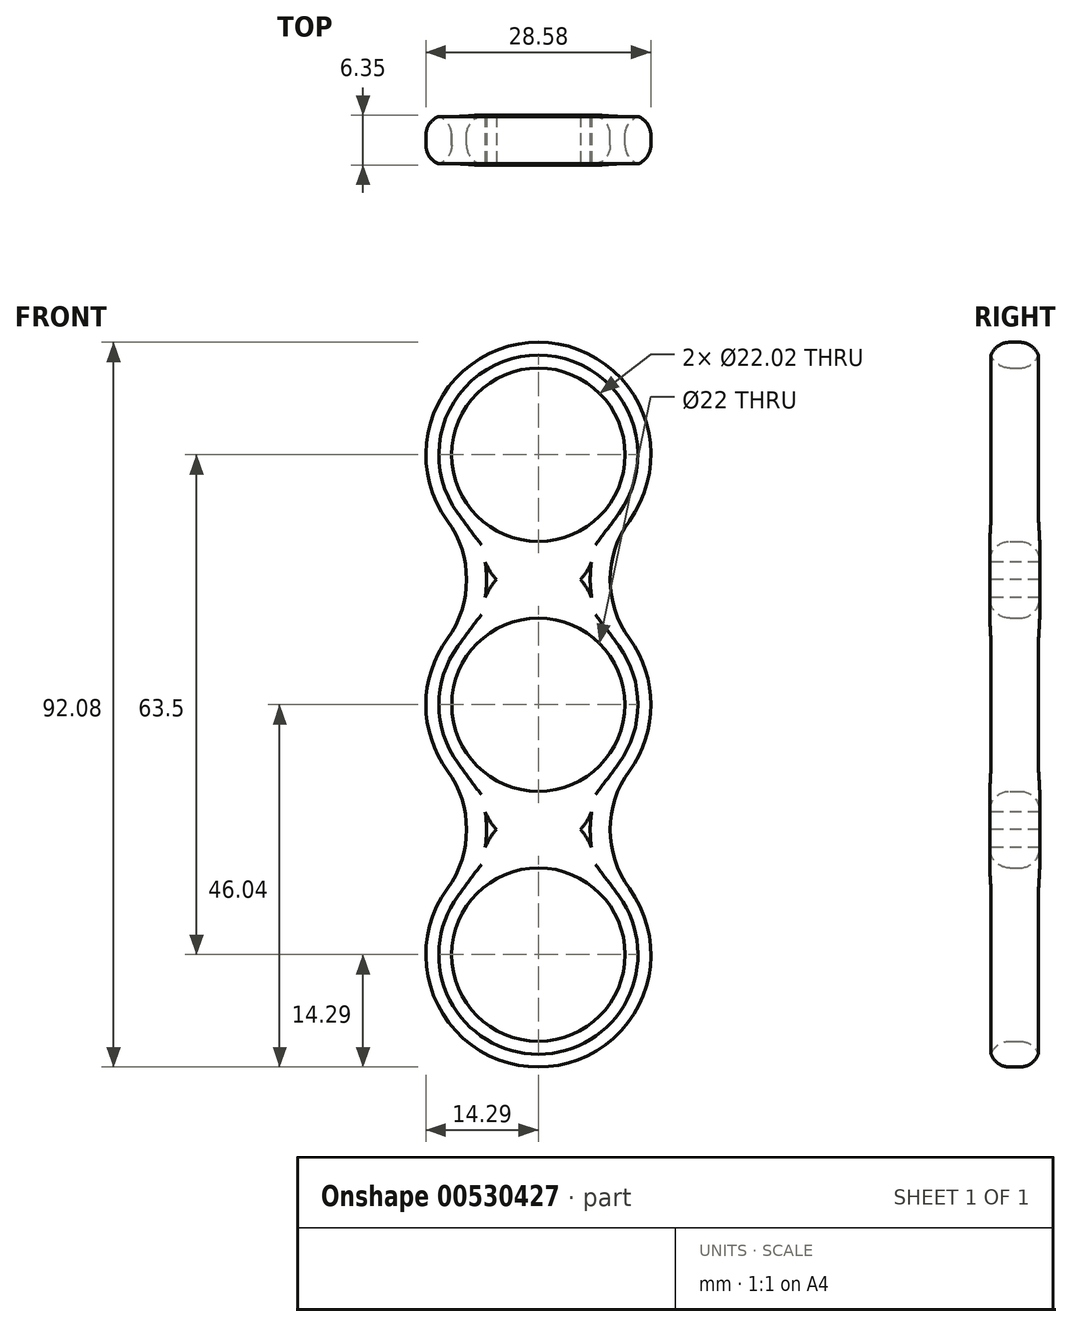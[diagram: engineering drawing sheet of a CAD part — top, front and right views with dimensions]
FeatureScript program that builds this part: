
annotation { "Feature Type Name" : "Feature", "Feature Type Description" : "" }
export const myFeature = defineFeature(function(context is Context, id is Id, definition is map)
    precondition{}
    {
        {
            var Q0;
            Q0=qCreatedBy(makeId("Front.planeOp"),FACE);
            var sketch = newSketch(context, id + "F0", { "sketchPlane" : qUnion([Q0])});
            skCircle(sketch, "E0", {"center": v(0, 0) * mm, "radius": 11 * mm});
            skCircle(sketch, "E1", {"center": v(0, 0) * mm, "radius": 14.29 * mm});
            skCircle(sketch, "E2", {"center": v(0, 31.75) * mm, "radius": 11.01 * mm});
            skCircle(sketch, "E3", {"center": v(0, 31.75) * mm, "radius": 14.29 * mm});
            skCircle(sketch, "E4", {"center": v(0, -31.75) * mm, "radius": 11.01 * mm});
            skCircle(sketch, "E5", {"center": v(0, -31.75) * mm, "radius": 14.29 * mm});
            skSolve(sketch);
        }
        {
            var Q0;
            Q0=makeQuery(id+"F0.imprint","IMPRINT",FACE,{"disambiguationData":[TD([[makeQuery(id+"F0.imprint","IMPRINT",EDGE,{"derivedFrom":sQuery(id+"F0.wireOp",EDGE,"E2")}),1.0]])]});
            var sketch = newSketch(context, id + "F1", { "sketchPlane" : qUnion([Q0])});
            skArc(sketch, "E6", {"start": v(-11.55, 8.4) * mm, "mid": v(-9.12, 15.88) * mm, "end": v(-11.55, 23.35) * mm});
            skArc(sketch, "E7", {"start": v(11.55, 23.35) * mm, "mid": v(9.12, 15.88) * mm, "end": v(11.55, 8.4) * mm});
            skArc(sketch, "E8", {"start": v(-11.55, -23.35) * mm, "mid": v(-9.12, -15.88) * mm, "end": v(-11.55, -8.4) * mm});
            skArc(sketch, "E9", {"start": v(11.55, -8.4) * mm, "mid": v(9.12, -15.88) * mm, "end": v(11.55, -23.35) * mm});
            skCircle(sketch, "E10.0", {"center": v(0, 0) * mm, "radius": 14.29 * mm});
            skCircle(sketch, "E11.0", {"center": v(0, 0) * mm, "radius": 11 * mm});
            skCircle(sketch, "E12.0", {"center": v(0, 31.75) * mm, "radius": 11.01 * mm});
            skCircle(sketch, "E13.0", {"center": v(0, 31.75) * mm, "radius": 14.29 * mm});
            skCircle(sketch, "E14.0", {"center": v(0, -31.75) * mm, "radius": 14.29 * mm});
            skCircle(sketch, "E15.0", {"center": v(0, -31.75) * mm, "radius": 11.01 * mm});
            skSolve(sketch);
        }
        {
            var Q0;
            Q0 = qSketchRegion(id + "F1", true);
            extrude(context, id + "F2", {"entities" : qUnion([Q0]), "depth" : 6.35 * mm, "offsetDistance" : 25.4 * mm});
        }
        {
            var Q0;
            Q0=makeQuery(id+"F2.opExtrude","CAP_FACE",FACE,{"disambiguationData":[OSD([sQuery(id+"F1.wireOp",EDGE,"E6"),sQuery(id+"F1.wireOp",EDGE,"E7"),sQuery(id+"F1.wireOp",EDGE,"E8"),sQuery(id+"F1.wireOp",EDGE,"E9"),sQuery(id+"F1.wireOp",EDGE,"E10.0"),sQuery(id+"F1.wireOp",EDGE,"E11.0"),sQuery(id+"F1.wireOp",EDGE,"E12.0"),sQuery(id+"F1.wireOp",EDGE,"E13.0"),sQuery(id+"F1.wireOp",EDGE,"E14.0"),sQuery(id+"F1.wireOp",EDGE,"E15.0")])],"isStart":false});
            fillet(context, id + "F3", {"entities" : qUnion([Q0]), "radius" : 2.54 * mm, "tangentPropagation" : true, "allowEdgeOverflow" : false});
        }
        {
            var Q0;
            Q0=makeQuery(id+"F2.opExtrude","CAP_FACE",FACE,{"disambiguationData":[OSD([sQuery(id+"F1.wireOp",EDGE,"E6"),sQuery(id+"F1.wireOp",EDGE,"E7"),sQuery(id+"F1.wireOp",EDGE,"E8"),sQuery(id+"F1.wireOp",EDGE,"E9"),sQuery(id+"F1.wireOp",EDGE,"E10.0"),sQuery(id+"F1.wireOp",EDGE,"E11.0"),sQuery(id+"F1.wireOp",EDGE,"E12.0"),sQuery(id+"F1.wireOp",EDGE,"E13.0"),sQuery(id+"F1.wireOp",EDGE,"E14.0"),sQuery(id+"F1.wireOp",EDGE,"E15.0")])],"isStart":true});
            fillet(context, id + "F4", {"entities" : qUnion([Q0]), "radius" : 2.54 * mm, "tangentPropagation" : true, "allowEdgeOverflow" : false});
        }
        {
            var Q0;
            Q0=makeQuery(id+"F3.opFillet","SPLIT",FACE,{"disambiguationData":[OD(0.0)],"derivedFrom":makeQuery(id+"F2.opExtrude","CAP_FACE",FACE,{"disambiguationData":[OSD([sQuery(id+"F1.wireOp",EDGE,"E6"),sQuery(id+"F1.wireOp",EDGE,"E7"),sQuery(id+"F1.wireOp",EDGE,"E8"),sQuery(id+"F1.wireOp",EDGE,"E9"),sQuery(id+"F1.wireOp",EDGE,"E10.0"),sQuery(id+"F1.wireOp",EDGE,"E11.0"),sQuery(id+"F1.wireOp",EDGE,"E12.0"),sQuery(id+"F1.wireOp",EDGE,"E13.0"),sQuery(id+"F1.wireOp",EDGE,"E14.0"),sQuery(id+"F1.wireOp",EDGE,"E15.0")])],"isStart":false})});
            var sketch = newSketch(context, id + "F5", { "sketchPlane" : qUnion([Q0])});
            skArc(sketch, "E16", {"start": v(7.25, 11.44) * mm, "mid": v(0, 18.2) * mm, "end": v(-7.25, 11.44) * mm});
            skArc(sketch, "E17", {"start": v(-7.24, 20.3) * mm, "mid": v(0, 13.54) * mm, "end": v(7.24, 20.3) * mm});
            skSolve(sketch);
        }
        {
            var Q0;
            {var subQ0=sQuery(id+"F5.wireOp",EDGE,"E17");var subQ1=sQuery(id+"F5.wireOp",EDGE,"E16");var subQ2=makeQuery(id+"F5.imprint","INTERSECT",VERTEX,{"disambiguationData":[OD(0.0)],"derivedFrom":[subQ1,subQ0]});Q0=makeQuery(id+"F5.imprint","IMPRINT",FACE,{"disambiguationData":[TD([[makeQuery(id+"F5.imprint","IMPRINT",EDGE,{"disambiguationData":[TD([[subQ2,1.0]])],"derivedFrom":subQ1}),-1.0]])]});}
            var Q1;
            {var subQ0=sQuery(id+"F5.wireOp",EDGE,"E17");var subQ1=sQuery(id+"F5.wireOp",EDGE,"E16");var subQ2=makeQuery(id+"F5.imprint","INTERSECT",VERTEX,{"disambiguationData":[OD(1.0)],"derivedFrom":[subQ1,subQ0]});Q1=makeQuery(id+"F5.imprint","IMPRINT",FACE,{"disambiguationData":[TD([[makeQuery(id+"F5.imprint","IMPRINT",EDGE,{"disambiguationData":[TD([[subQ2,-1.0]])],"derivedFrom":subQ1}),-1.0]])]});}
            extrude(context, id + "F6", {"entities" : qUnion([Q0, Q1]), "operationType" : NewBodyOperationType.REMOVE, "endBound" : BoundingType.THROUGH_ALL, "oppositeDirection" : true, "depth" : 25.4 * mm, "offsetDistance" : 25.4 * mm});
        }
        {
            var Q0;
            Q0=makeQuery(id+"F3.opFillet","SPLIT",FACE,{"disambiguationData":[OD(1.0)],"derivedFrom":makeQuery(id+"F2.opExtrude","CAP_FACE",FACE,{"disambiguationData":[OSD([sQuery(id+"F1.wireOp",EDGE,"E6"),sQuery(id+"F1.wireOp",EDGE,"E7"),sQuery(id+"F1.wireOp",EDGE,"E8"),sQuery(id+"F1.wireOp",EDGE,"E9"),sQuery(id+"F1.wireOp",EDGE,"E10.0"),sQuery(id+"F1.wireOp",EDGE,"E11.0"),sQuery(id+"F1.wireOp",EDGE,"E12.0"),sQuery(id+"F1.wireOp",EDGE,"E13.0"),sQuery(id+"F1.wireOp",EDGE,"E14.0"),sQuery(id+"F1.wireOp",EDGE,"E15.0")])],"isStart":false})});
            var sketch = newSketch(context, id + "F7", { "sketchPlane" : qUnion([Q0])});
            skArc(sketch, "E18", {"start": v(7.24, -20.3) * mm, "mid": v(0, -13.54) * mm, "end": v(-7.24, -20.3) * mm});
            skArc(sketch, "E19", {"start": v(-7.25, -11.44) * mm, "mid": v(0, -18.2) * mm, "end": v(7.25, -11.44) * mm});
            skSolve(sketch);
        }
        {
            var Q0;
            {var subQ0=sQuery(id+"F7.wireOp",EDGE,"E19");var subQ1=sQuery(id+"F7.wireOp",EDGE,"E18");var subQ2=makeQuery(id+"F7.imprint","INTERSECT",VERTEX,{"disambiguationData":[OD(1.0)],"derivedFrom":[subQ1,subQ0]});Q0=makeQuery(id+"F7.imprint","IMPRINT",FACE,{"disambiguationData":[TD([[makeQuery(id+"F7.imprint","IMPRINT",EDGE,{"disambiguationData":[TD([[subQ2,-1.0]])],"derivedFrom":subQ1}),-1.0]])]});}
            var Q1;
            {var subQ0=sQuery(id+"F7.wireOp",EDGE,"E19");var subQ1=sQuery(id+"F7.wireOp",EDGE,"E18");var subQ2=makeQuery(id+"F7.imprint","INTERSECT",VERTEX,{"disambiguationData":[OD(0.0)],"derivedFrom":[subQ1,subQ0]});Q1=makeQuery(id+"F7.imprint","IMPRINT",FACE,{"disambiguationData":[TD([[makeQuery(id+"F7.imprint","IMPRINT",EDGE,{"disambiguationData":[TD([[subQ2,1.0]])],"derivedFrom":subQ1}),-1.0]])]});}
            extrude(context, id + "F8", {"entities" : qUnion([Q0, Q1]), "operationType" : NewBodyOperationType.REMOVE, "endBound" : BoundingType.THROUGH_ALL, "oppositeDirection" : true, "depth" : 25.4 * mm, "offsetDistance" : 25.4 * mm});
        }
    });
